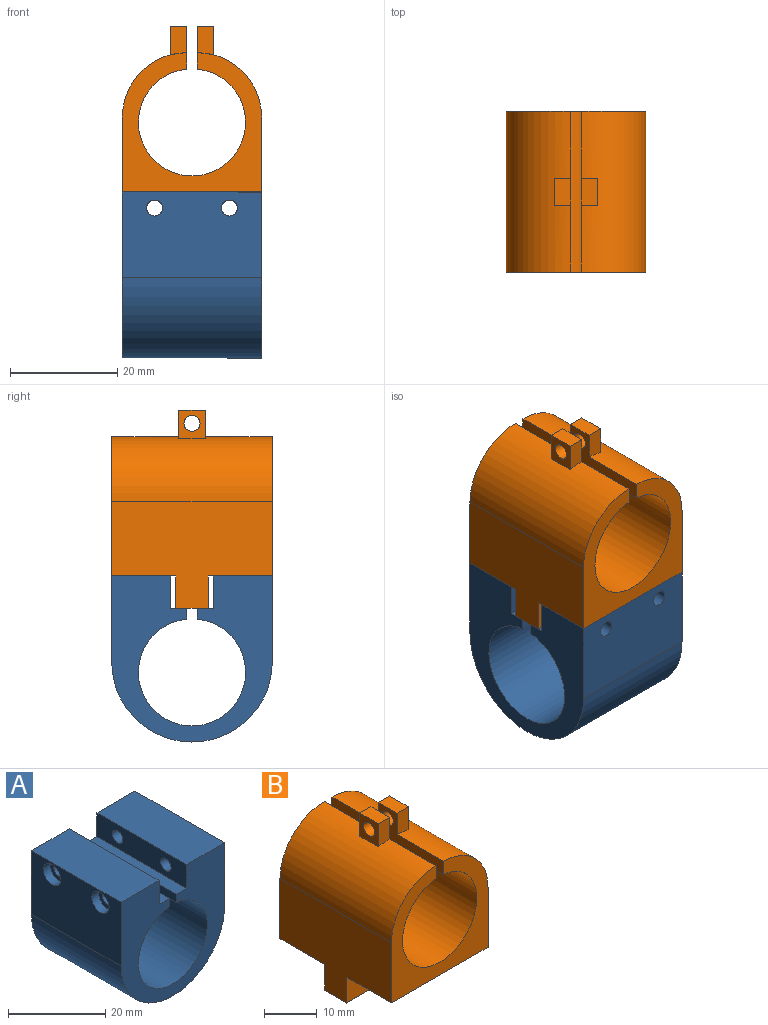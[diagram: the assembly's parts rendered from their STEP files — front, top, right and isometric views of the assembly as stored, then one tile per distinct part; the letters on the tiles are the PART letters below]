
ASSEMBLY  parts=2 mates=1
PART A: 22 faces, bbox 30x26x31 mm
  f0: plane 26x11mm, normal (0,0,1), area 286mm2, adj f1,f9,f10,f11
  f1: plane 26x6mm, normal (-1,0,0), area 141.9mm2, adj f0,f2,f10,f11,f14,f15
  f2: plane 26x3mm, normal (0,0,1), area 78mm2, adj f1,f3,f10,f11
  f3: plane 26x2.05mm, normal (-1,0,0), area 53.3mm2, adj f2,f10,f11,f12
  f4: plane 26x2.05mm, normal (1,0,0), area 53.3mm2, adj f5,f10,f11,f12
  f5: plane 26x3mm, normal (0,0,1), area 78mm2, adj f4,f6,f10,f11
  f6: plane 26x6mm, normal (1,0,0), area 141.9mm2, adj f5,f7,f10,f11,f16,f19
  f7: plane 26x11mm, normal (0,0,1), area 286mm2, adj f6,f8,f10,f11
  f8: plane 26x16mm, normal (-1,0,0), area 376.7mm2, adj f7,f10,f11,f13,f18,f21
  f9: plane 26x16mm, normal (1,0,0), area 401.9mm2, adj f0,f10,f11,f13,f14,f15
  f10: plane 31x30mm, normal (0,-1,0), area 467.2mm2, adj f0,f1,f2,f3,f4,f5,f6,f7
  f11: plane 31x30mm, normal (0,1,0), area 467.2mm2, adj f0,f1,f2,f3,f4,f5,f6,f7
  f12: cylinder r=10mm len=26mm, axis (0,-1,0), area 1581.5mm2, adj f3,f4,f10,f11
  f13: cylinder r=15mm len=30mm, axis (0,1,0), area 1225.2mm2, adj f8,f9,f10,f11
  f14: cylinder r=1.5mm len=11mm, axis (-1,0,0), area 103.7mm2, adj f1,f9
  f15: cylinder r=1.5mm len=11mm, axis (-1,0,0), area 103.7mm2, adj f1,f9
  f16: cylinder r=1.5mm len=9mm, axis (-1,0,0), area 84.8mm2, adj f6,f17
  f17: plane 5x5mm, normal (-1,0,0), area 12.6mm2, adj f16,f18
  f18: cylinder r=2.5mm len=5mm, axis (-1,0,0), area 31.4mm2, adj f8,f17
  f19: cylinder r=1.5mm len=9mm, axis (-1,0,0), area 84.8mm2, adj f6,f20
  f20: plane 5x5mm, normal (-1,0,0), area 12.6mm2, adj f19,f21
  f21: cylinder r=2.5mm len=5mm, axis (-1,0,0), area 31.4mm2, adj f8,f20
PART B: 26 faces, bbox 26x30x37 mm
  f0: plane 30x8.05mm, normal (1,0,0), area 109.4mm2, adj f1,f3,f4,f5,f11,f12,f13,f25
  f1: plane 5x3mm, normal (0,0,1), area 15mm2, adj f0,f2,f3,f4
  f2: plane 5.38x5mm, normal (-1,0,0), area 19.8mm2, adj f1,f3,f4,f5,f25
  f3: plane 5.38x3mm, normal (0,-1,0), area 15.4mm2, adj f0,f1,f2,f5
  f4: plane 5.38x3mm, normal (0,1,0), area 15.4mm2, adj f0,f1,f2,f5
  f5: cylinder r=12mm len=30mm, axis (0,1,0), area 550.3mm2, adj f0,f2,f3,f4,f7,f12,f13
  f6: plane 26x12mm, normal (0,0,-1), area 312mm2, adj f7,f9,f12,f16
  f7: plane 30x20mm, normal (-1,0,0), area 456mm2, adj f5,f6,f8,f12,f13,f15,f16,f17
  f8: plane 26x12mm, normal (0,0,-1), area 312mm2, adj f7,f9,f13,f15
  f9: plane 30x20mm, normal (1,0,0), area 456mm2, adj f6,f8,f12,f13,f14,f15,f16,f17
  f10: plane 30x8.05mm, normal (-1,0,0), area 109.4mm2, adj f11,f12,f13,f14,f21,f22,f23,f24
  f11: cylinder r=10mm len=30mm, axis (0,1,0), area 1824.9mm2, adj f0,f10,f12,f13
  f12: plane 26x26mm, normal (0,-1,0), area 294mm2, adj f0,f5,f6,f7,f9,f10,f11,f14
  f13: plane 26x26mm, normal (0,1,0), area 294mm2, adj f0,f5,f7,f8,f9,f10,f11,f14
  f14: cylinder r=12mm len=30mm, axis (0,-1,0), area 550.3mm2, adj f9,f10,f12,f13,f20,f22,f23
  f15: plane 26x6mm, normal (0,1,0), area 141.9mm2, adj f7,f8,f9,f17,f18,f19
  f16: plane 26x6mm, normal (0,-1,0), area 141.9mm2, adj f6,f7,f9,f17,f18,f19
  f17: plane 26x6mm, normal (0,0,-1), area 156mm2, adj f7,f9,f15,f16
  f18: cylinder r=1.5mm len=6mm, axis (0,-1,0), area 56.5mm2, adj f15,f16
  f19: cylinder r=1.5mm len=6mm, axis (0,-1,0), area 56.5mm2, adj f15,f16
  f20: plane 5.38x5mm, normal (1,0,0), area 19.8mm2, adj f14,f21,f22,f23,f24
  f21: plane 5x3mm, normal (0,0,1), area 15mm2, adj f10,f20,f22,f23
  f22: plane 5.38x3mm, normal (0,-1,0), area 15.4mm2, adj f10,f14,f20,f21
  f23: plane 5.38x3mm, normal (0,1,0), area 15.4mm2, adj f10,f14,f20,f21
  f24: cylinder r=1.5mm len=3mm, axis (1,0,0), area 28.3mm2, adj f10,f20
  f25: cylinder r=1.5mm len=3mm, axis (1,0,0), area 28.3mm2, adj f0,f2
PLACE A rot(axis=(0,0,-1),90deg) t=(-8.33,2.1,-30)mm fixed
PLACE B rot(axis=(0,0,1),0deg) t=(-8.33,2.1,1)mm
MATE slider A.f11 <-> B.f9  axis (1,0,0) through (4.67,17.1,1)mm
